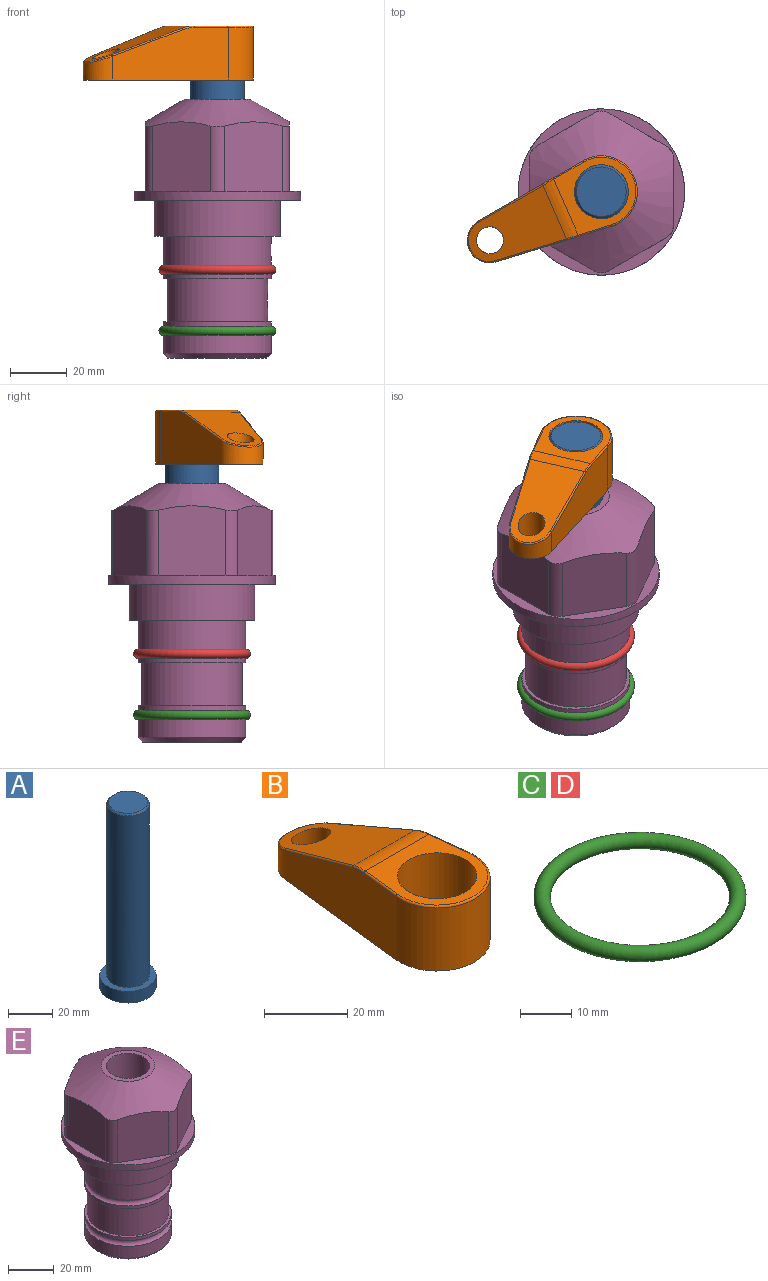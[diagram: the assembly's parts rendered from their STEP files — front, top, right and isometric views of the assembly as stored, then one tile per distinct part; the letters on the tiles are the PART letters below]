
ASSEMBLY  parts=5 mates=3
PART A: 6 faces, bbox 25.4x25.4x101.6 mm
  f0: plane 17.46x17.46mm, normal (0,0,1), area 239.5mm2, adj f5
  f1: plane 25.4x25.4mm, normal (0,0,-1), area 506.7mm2, adj f2
  f2: cylinder r=12.7mm len=25.4mm, axis (0,0,1), area 506.7mm2, adj f1,f3
  f3: plane 25.4x25.4mm, normal (0,0,1), area 221.7mm2, adj f2,f4
  f4: cylinder r=9.53mm len=94.46mm, axis (0,0,1), area 5653mm2, adj f3,f5
  f5: cone r=8.73mm half-angle=45deg, axis (0,0,-1), area 64.4mm2, adj f0,f4
PART B: 44 faces, bbox 27.5x64.5x19.1 mm
  f0: plane 2.3x0.95mm, normal (0,0,-1), area 1mm2, adj f25,f30,f34
  f1: plane 63.5x25.4mm, normal (0,0,-1), area 561.7mm2, adj f2,f3,f4,f5,f6,f7,f19,f20
  f2: cylinder r=12.7mm len=25.4mm, axis (0,0,-1), area 792.2mm2, adj f1,f3,f5,f13
  f3: plane 42.33x18.54mm, normal (0.99,0.11,0), area 647mm2, adj f1,f2,f4,f11,f12,f14
  f4: cylinder r=7.94mm len=15.78mm, axis (0,0,-1), area 158.6mm2, adj f1,f3,f5,f16
  f5: plane 42.33x18.54mm, normal (-0.99,0.11,0), area 647mm2, adj f1,f2,f4,f15,f17,f18
  f6: cylinder r=9.53mm len=19.05mm, axis (0,0,-1), area 1140.1mm2, adj f1,f8
  f7: cylinder r=4.76mm len=10.98mm, axis (0,0,-1), area 276.1mm2, adj f1,f9
  f8: plane 25.83x24.38mm, normal (0,0,1), area 262.2mm2, adj f6,f10,f11,f13,f15
  f9: plane 32.49x20.55mm, normal (0,0.34,0.94), area 489.9mm2, adj f7,f10,f14,f16,f18
  f10: cylinder r=12.7mm len=21.49mm, axis (-1,0,0), area 93.2mm2, adj f8,f9,f12,f17
  f11: cylinder r=0.51mm len=12.34mm, axis (0.11,-0.99,0), area 9.9mm2, adj f3,f8,f12,f13
  f12: bspline ~7.62x1.64mm, area 3.5mm2, adj f3,f10,f11,f14
  f13: torus R=12.19mm, axis (0,0,1), area 33.6mm2, adj f2,f8,f11,f15
  f14: cylinder r=0.51mm len=26.01mm, axis (0.1,-0.93,0.34), area 21.6mm2, adj f3,f9,f12,f16
  f15: cylinder r=0.51mm len=12.34mm, axis (0.11,0.99,0), area 9.9mm2, adj f5,f8,f13,f17
  f16: bspline ~15.78x7.05mm, area 15.7mm2, adj f4,f9,f14,f18
  f17: bspline ~7.62x1.64mm, area 3.5mm2, adj f5,f10,f15,f18
  f18: cylinder r=0.51mm len=26.01mm, axis (0.1,0.93,-0.34), area 21.6mm2, adj f5,f9,f16,f17
  f19: plane 21.6x14.29mm, normal (-0.99,-0.11,0), area 242.6mm2, adj f1,f26,f28,f34,f36,f38
  f20: plane 21.6x14.29mm, normal (0.99,-0.11,0), area 242.6mm2, adj f1,f27,f29,f37,f39,f41
  f21: cylinder r=12.7mm len=14.29mm, axis (0,0,-1), area 173.2mm2, adj f1,f26,f27,f30,f31,f33
  f22: cylinder r=7.94mm len=7.63mm, axis (0,0,-1), area 53.8mm2, adj f1,f28,f29,f42
  f23: plane 2.3x0.95mm, normal (0,0,-1), area 1mm2, adj f25,f33,f37
  f24: plane 17.94x12.32mm, normal (0,-0.34,-0.94), area 191.2mm2, adj f25,f38,f41,f42
  f25: cylinder r=9.53mm len=12.93mm, axis (-1,0,0), area 37.5mm2, adj f0,f23,f24,f31,f36,f39
  f26: cylinder r=1.59mm len=14.29mm, axis (0,0,-1), area 49mm2, adj f1,f19,f21,f32
  f27: cylinder r=1.59mm len=14.29mm, axis (0,0,-1), area 49mm2, adj f1,f20,f21,f35
  f28: cylinder r=1.59mm len=7.28mm, axis (0,0,-1), area 22.1mm2, adj f1,f19,f22,f40
  f29: cylinder r=1.59mm len=7.28mm, axis (0,0,-1), area 22.1mm2, adj f1,f20,f22,f43
  f30: torus R=14.29mm, axis (0,0,1), area 5.8mm2, adj f0,f21,f31,f32
  f31: bspline ~11.06x2.73mm, area 20.8mm2, adj f21,f25,f30,f33
  f32: sphere r=1.59mm, area 5.4mm2, adj f26,f30,f34
  f33: torus R=14.29mm, axis (0,0,1), area 5.8mm2, adj f21,f23,f31,f35
  f34: cylinder r=1.59mm len=1.68mm, axis (-0.11,0.99,0), area 2.4mm2, adj f0,f19,f32,f36
  f35: sphere r=1.59mm, area 5.4mm2, adj f27,f33,f37
  f36: bspline ~5.82x2.33mm, area 7.7mm2, adj f19,f25,f34,f38
  f37: cylinder r=1.59mm len=1.68mm, axis (0.11,0.99,0), area 2.4mm2, adj f20,f23,f35,f39
  f38: cylinder r=1.59mm len=18.33mm, axis (0.1,-0.93,0.34), area 46.7mm2, adj f19,f24,f36,f40
  f39: bspline ~5.82x2.33mm, area 7.7mm2, adj f20,f25,f37,f41
  f40: sphere r=1.59mm, area 3.6mm2, adj f28,f38,f42
  f41: cylinder r=1.59mm len=18.33mm, axis (0.1,0.93,-0.34), area 46.7mm2, adj f20,f24,f39,f43
  f42: bspline ~8.31x1.84mm, area 15.3mm2, adj f22,f24,f40,f43
  f43: sphere r=1.59mm, area 3.6mm2, adj f29,f41,f42
PART C: 1 faces, bbox 44.7x44.7x3.2 mm
  f0: torus R=19.05mm, axis (0,0,1), area 1193.9mm2
PART D: same geometry as C
PART E: 36 faces, bbox 58.7x58.7x91.2 mm
  f0: cylinder r=17.78mm len=35.56mm, axis (0,0,1), area 1670.8mm2, adj f23,f24,f31
  f1: cylinder r=19.05mm len=38.1mm, axis (0,0,1), area 1191.9mm2, adj f26,f27,f30
  f2: plane 58.66x58.66mm, normal (0,0,-1), area 1150.6mm2, adj f3,f28
  f3: cylinder r=29.33mm len=58.66mm, axis (0,0,-1), area 585.1mm2, adj f2,f4
  f4: plane 58.66x58.66mm, normal (0,0,1), area 475.9mm2, adj f3,f5,f6,f7,f8,f9,f10,f11
  f5: plane 24.5x20.32mm, normal (-0.5,0.87,0), area 562.8mm2, adj f4,f15,f16,f17
  f6: plane 24.5x20.32mm, normal (0.5,0.87,0), area 562.8mm2, adj f4,f14,f15,f17
  f7: plane 24.5x23.48mm, normal (1,0,0), area 562.8mm2, adj f4,f13,f14,f17
  f8: plane 24.5x20.32mm, normal (0.5,-0.87,0), area 562.8mm2, adj f4,f12,f13,f17
  f9: plane 24.5x20.32mm, normal (-0.5,-0.87,0), area 562.8mm2, adj f4,f11,f12,f17
  f10: plane 24.5x23.48mm, normal (-1,0,0), area 562.8mm2, adj f4,f11,f16,f17
  f11: cylinder r=5.08mm len=23.01mm, axis (0,0,-1), area 121.2mm2, adj f4,f9,f10,f17
  f12: cylinder r=5.08mm len=23.01mm, axis (0,0,-1), area 121.2mm2, adj f4,f8,f9,f17
  f13: cylinder r=5.08mm len=23.01mm, axis (0,0,-1), area 121.2mm2, adj f4,f7,f8,f17
  f14: cylinder r=5.08mm len=23.01mm, axis (0,0,-1), area 121.2mm2, adj f4,f6,f7,f17
  f15: cylinder r=5.08mm len=23.01mm, axis (0,0,-1), area 121.2mm2, adj f4,f5,f6,f17
  f16: cylinder r=5.08mm len=23.01mm, axis (0,0,-1), area 121.2mm2, adj f4,f5,f10,f17
  f17: cone r=11.73mm half-angle=60deg, axis (0,0,-1), area 2071.8mm2, adj f5,f6,f7,f8,f9,f10,f11,f12
  f18: plane 23.46x23.46mm, normal (0,0,1), area 147.4mm2, adj f17,f35
  f19: plane 34.93x34.93mm, normal (0,0,-1), area 958mm2, adj f29
  f20: cylinder r=19.05mm len=38.1mm, axis (0,0,1), area 760.1mm2, adj f21,f29
  f21: torus R=19.05mm, axis (0,0,1), area 565.3mm2, adj f20,f22
  f22: cylinder r=19.05mm len=38.1mm, axis (0,0,1), area 190mm2, adj f21,f23
  f23: plane 38.1x38.1mm, normal (0,0,1), area 146.9mm2, adj f0,f22
  f24: plane 38.1x38.1mm, normal (0,0,-1), area 146.9mm2, adj f0,f25
  f25: cylinder r=19.05mm len=38.1mm, axis (0,0,1), area 190mm2, adj f24,f26
  f26: torus R=19.05mm, axis (0,0,1), area 565.3mm2, adj f1,f25
  f27: plane 44.45x44.45mm, normal (0,0,-1), area 411.7mm2, adj f1,f28
  f28: cylinder r=22.23mm len=44.45mm, axis (0,0,1), area 1773.5mm2, adj f2,f27
  f29: cone r=19.05mm half-angle=45deg, axis (0,0,1), area 257.5mm2, adj f19,f20
  f30: cylinder r=3.17mm len=6.75mm, axis (-1,0,0), area 128mm2, adj f1,f33
  f31: cylinder r=3.17mm len=6.35mm, axis (-1,0,0), area 102.5mm2, adj f0,f33
  f32: plane 25.4x25.4mm, normal (0,0,1), area 506.7mm2, adj f33
  f33: cylinder r=12.7mm len=66.42mm, axis (0,0,-1), area 5236.2mm2, adj f30,f31,f32,f34
  f34: cone r=9.53mm half-angle=30deg, axis (0,0,-1), area 443.4mm2, adj f33,f35
  f35: cylinder r=9.53mm len=19.05mm, axis (0,0,-1), area 849mm2, adj f18,f34
PLACE A rot(axis=(0,0,-1),156.5deg) t=(0,0,-12.21)mm
PLACE B rot(axis=(0,0,1),113.5deg) t=(0,0,42.4)mm
PLACE C t=(0,0,-21.59)mm
PLACE D at identity
PLACE E at identity fixed
MATE fastened C.f0 <-> E.f0  axis (0,0,1) through (0,0,-46.1)mm
MATE cylindrical A.f2 <-> E.f0  axis (0,0,1) through (0,0,13.43)mm
MATE fastened B.f2 <-> A.f2  axis (0,0,1) through (0,0,61.45)mm
